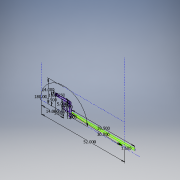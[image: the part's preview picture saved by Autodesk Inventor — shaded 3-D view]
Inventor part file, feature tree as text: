
AUTODESK INVENTOR PART (.ipt)
format: ipt  version: 2017 SP1 (Build 210196100, 196)  size: 117,760 bytes
history: native  units: in
note: dims shown in document units (in); Inventor stores cm internally (conversion verified against a paired STEP export)
features: sketch x1
ambient origin geometry x8: Origin, YZ Plane, XZ Plane, XY Plane, X Axis, Y Axis, Z Axis, Center Point
feature tree (1):
  sketch  "Sketch1"  dims[d0=5.0in d1=2.0in d3=1.0in d4=5.0in d5=7.5in d7=8.25in d10=1.25in d11=3.25in d13=39.5in d16=14.0in d21=8.0in d22=0.0in d32=1.0in d35=0.75in d36=1.5in d37=30.0in d38=14.0in d39=52.0in]
